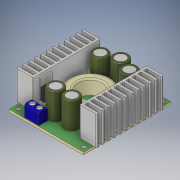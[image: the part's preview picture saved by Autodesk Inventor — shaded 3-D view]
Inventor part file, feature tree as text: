
AUTODESK INVENTOR PART (.ipt)
format: ipt  version: 2019 (Build 230136000, 136)  size: 680,448 bytes
history: native  units: mm
features: sketch x11, extrude x10, projected_geometry x5, fillet x3, other x1, hole x1, mirror x1, chamfer x1
ambient origin geometry x8: Origin, YZ Plane, XZ Plane, XY Plane, X Axis, Y Axis, Z Axis, Center Point
bodies: Body1 (feature_tree)
feature tree (33):
  other  "Твердое тело1"
  extrude  "Выдавливание1"  Depth=60.0mm
  hole  "Отверстие1"  [1 undecoded]
  extrude  "Выдавливание2"  Depth=1.6mm TaperAngle=0.0deg
  extrude  "Выдавливание3"  Depth=3.0mm
  fillet  "Сопряжение1"  Radius=3.0mm
  extrude  "Выдавливание4"  Depth=1.6mm
  extrude  "Выдавливание5"  Depth=46.0mm
  extrude  "Выдавливание6"  Depth=10.0mm
  extrude  "Выдавливание7"  Depth=2.0mm
  extrude  "Выдавливание8"  Depth=60.0mm
  fillet  "Сопряжение2"  Radius=20.0mm
  mirror  "Зеркальное отражение1"
  fillet  "Сопряжение3"  Radius=5.0mm
  extrude  "Выдавливание9"  Depth=17.0mm
  extrude  "Выдавливание10"  Depth=10.0mm TaperAngle=0.0deg
  chamfer  "Фаска1"  Distance=1.0mm
  sketch  "Эскиз1"
  sketch  "Эскиз2"
  sketch  "Эскиз3"
  sketch  "Эскиз4"
  sketch  "Эскиз5"
  sketch  "Эскиз6"
  projected_geometry  "Спроецированная петля1"
  projected_geometry  "Спроецированная петля2"
  projected_geometry  "Спроецированная петля3"
  projected_geometry  "Спроецированная петля4"
  projected_geometry  "Спроецированная петля5"
  sketch  "Эскиз8"
  sketch  "Эскиз9"
  sketch  "Эскиз10"
  sketch  "Эскиз11"
  sketch  "Эскиз12"
note: 1 required parameter value undecoded (feature->parameter linkage not recoverable at this tier; creation-order binding heuristic only, values carry confidence <= 0.55)
